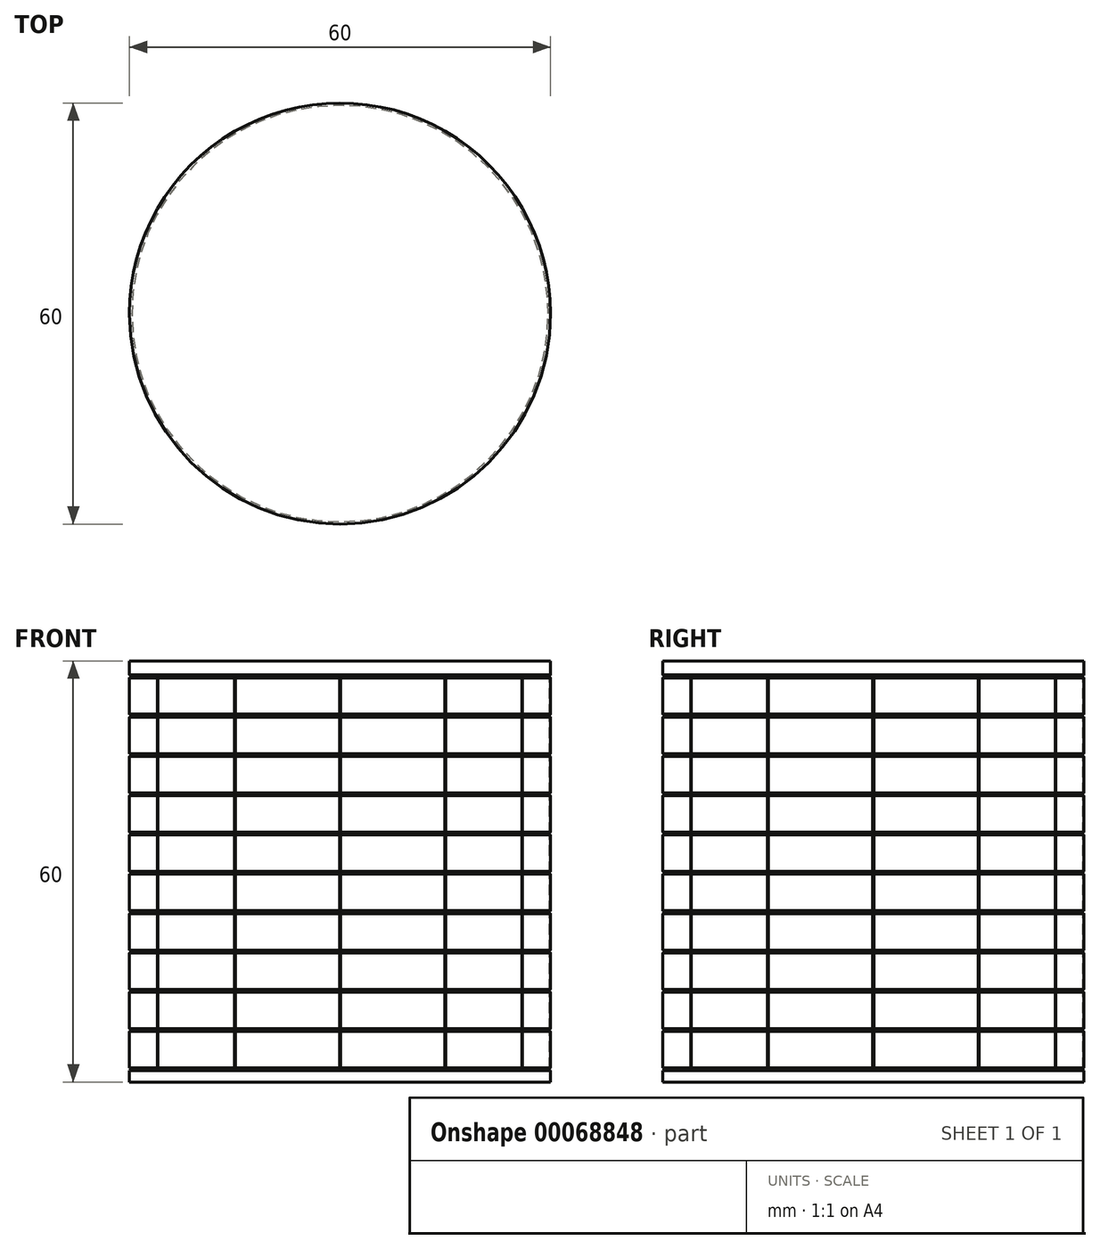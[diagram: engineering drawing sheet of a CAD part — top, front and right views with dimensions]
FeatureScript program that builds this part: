
annotation { "Feature Type Name" : "Feature", "Feature Type Description" : "" }
export const myFeature = defineFeature(function(context is Context, id is Id, definition is map)
    precondition{}
    {
        {
            var Q0;
            Q0=qCreatedBy(makeId("Top.planeOp"),FACE);
            var sketch = newSketch(context, id + "F0", { "sketchPlane" : qUnion([Q0])});
            skCircle(sketch, "E0", {"center": v(0, 0) * mm, "radius": 30 * mm});
            skPoint(sketch, "E1", {"position": v(0, -30) * mm});
            skSolve(sketch);
        }
        {
            var Q0;
            Q0=makeQuery(id+"F0.imprint","IMPRINT",FACE,{"disambiguationData":[TD([[makeQuery(id+"F0.imprint","IMPRINT",EDGE,{"derivedFrom":sQuery(id+"F0.wireOp",EDGE,"E0")}),1.0]])]});
            extrude(context, id + "F1", {"entities" : qUnion([Q0]), "depth" : 60 * mm});
        }
        {
            var Q0;
            Q0=makeQuery(id+"F1.opExtrude","CAP_FACE",FACE,{"disambiguationData":[OSD([sQuery(id+"F0.wireOp",EDGE,"E0")])],"isStart":false});
            var sketch = newSketch(context, id + "F2", { "sketchPlane" : qUnion([Q0])});
            skLineSegment(sketch, "E2", {"start": v(0, -29.87) * mm, "end": v(-0.08, -30) * mm});
            skLineSegment(sketch, "E3", {"start": v(-0.08, -30) * mm, "end": v(0.07, -30) * mm});
            skLineSegment(sketch, "E4", {"start": v(0.07, -30) * mm, "end": v(0, -29.87) * mm});
            skPoint(sketch, "E5", {"position": v(0, -30) * mm});
            skSolve(sketch);
        }
        {
            var Q0;
            Q0 = qSketchRegion(id + "F2", true);
            extrude(context, id + "F3", {"entities" : qUnion([Q0]), "operationType" : NewBodyOperationType.REMOVE, "oppositeDirection" : true, "depth" : 58 * mm, "hasSecondDirection" : true, "secondDirectionOppositeDirection" : true, "secondDirectionDepth" : 2 * mm});
        }
        {
            var Q0;
            Q0=makeQuery(id+"F3.boolean.opBoolean","COPY",FACE,{"derivedFrom":makeQuery(id+"F3.opExtrude","SWEPT_FACE",FACE,{"disambiguationData":[OSD([sQuery(id+"F2.wireOp",EDGE,"E2")])]})});
            var Q1;
            Q1=makeQuery(id+"F3.boolean.opBoolean","COPY",FACE,{"derivedFrom":makeQuery(id+"F3.opExtrude","CAP_FACE",FACE,{"disambiguationData":[OSD([sQuery(id+"F2.wireOp",EDGE,"E2"),sQuery(id+"F2.wireOp",EDGE,"E3"),sQuery(id+"F2.wireOp",EDGE,"E4")])],"isStart":true})});
            var Q2;
            Q2=makeQuery(id+"F3.boolean.opBoolean","COPY",FACE,{"derivedFrom":makeQuery(id+"F3.opExtrude","CAP_FACE",FACE,{"disambiguationData":[OSD([sQuery(id+"F2.wireOp",EDGE,"E2"),sQuery(id+"F2.wireOp",EDGE,"E3"),sQuery(id+"F2.wireOp",EDGE,"E4")])],"isStart":false})});
            var Q3;
            Q3=makeQuery(id+"F3.boolean.opBoolean","COPY",FACE,{"derivedFrom":makeQuery(id+"F3.opExtrude","SWEPT_FACE",FACE,{"disambiguationData":[OSD([sQuery(id+"F2.wireOp",EDGE,"E4")])]})});
            var Q4;
            Q4=makeQuery(id+"F1.opExtrude","CAP_EDGE",EDGE,{"disambiguationData":[OSD([sQuery(id+"F0.wireOp",EDGE,"E0")])],"isStart":true});
            circularPattern(context, id + "F4", {"faces" : qUnion([Q0, Q1, Q2, Q3]), "axis" : qUnion([Q4]), "angle" : 360 * degree, "instanceCount" : 12, "equalSpace" : true, "patternType" : PatternType.FACE});
        }
        {
            var Q0;
            Q0=qCreatedBy(makeId("Right.planeOp"),FACE);
            var sketch = newSketch(context, id + "F5", { "sketchPlane" : qUnion([Q0])});
            skLineSegment(sketch, "E6", {"start": v(-30, 58) * mm, "end": v(-30, 57.6) * mm});
            skLineSegment(sketch, "E7", {"start": v(-30, 57.6) * mm, "end": v(-29.65, 57.8) * mm});
            skLineSegment(sketch, "E8", {"start": v(-29.65, 57.8) * mm, "end": v(-30, 58) * mm});
            skLineSegment(sketch, "E9", {"start": v(-30, 58) * mm, "end": v(-30.1, 58) * mm});
            skLineSegment(sketch, "E10", {"start": v(-30.1, 58) * mm, "end": v(-30.1, 57.6) * mm});
            skLineSegment(sketch, "E11", {"start": v(-30.1, 57.6) * mm, "end": v(-30, 57.6) * mm});
            skLineSegment(sketch, "E12.0.1.0", {"start": v(-30.1, 52.4) * mm, "end": v(-30.1, 52) * mm});
            skLineSegment(sketch, "E12.0.1.1", {"start": v(-30, 52.4) * mm, "end": v(-30, 52) * mm});
            skLineSegment(sketch, "E12.0.1.2", {"start": v(-29.65, 52.2) * mm, "end": v(-30, 52.4) * mm});
            skLineSegment(sketch, "E12.0.1.3", {"start": v(-30, 52.4) * mm, "end": v(-30.1, 52.4) * mm});
            skLineSegment(sketch, "E12.0.1.4", {"start": v(-30, 52) * mm, "end": v(-29.65, 52.2) * mm});
            skLineSegment(sketch, "E12.0.1.5", {"start": v(-30.1, 52) * mm, "end": v(-30, 52) * mm});
            skLineSegment(sketch, "E12.0.2.0", {"start": v(-30.1, 46.8) * mm, "end": v(-30.1, 46.4) * mm});
            skLineSegment(sketch, "E12.0.2.1", {"start": v(-30, 46.8) * mm, "end": v(-30, 46.4) * mm});
            skLineSegment(sketch, "E12.0.2.2", {"start": v(-29.65, 46.6) * mm, "end": v(-30, 46.8) * mm});
            skLineSegment(sketch, "E12.0.2.3", {"start": v(-30, 46.8) * mm, "end": v(-30.1, 46.8) * mm});
            skLineSegment(sketch, "E12.0.2.4", {"start": v(-30, 46.4) * mm, "end": v(-29.65, 46.6) * mm});
            skLineSegment(sketch, "E12.0.2.5", {"start": v(-30.1, 46.4) * mm, "end": v(-30, 46.4) * mm});
            skLineSegment(sketch, "E12.0.3.0", {"start": v(-30.1, 41.2) * mm, "end": v(-30.1, 40.8) * mm});
            skLineSegment(sketch, "E12.0.3.1", {"start": v(-30, 41.2) * mm, "end": v(-30, 40.8) * mm});
            skLineSegment(sketch, "E12.0.3.2", {"start": v(-29.65, 41) * mm, "end": v(-30, 41.2) * mm});
            skLineSegment(sketch, "E12.0.3.3", {"start": v(-30, 41.2) * mm, "end": v(-30.1, 41.2) * mm});
            skLineSegment(sketch, "E12.0.3.4", {"start": v(-30, 40.8) * mm, "end": v(-29.65, 41) * mm});
            skLineSegment(sketch, "E12.0.3.5", {"start": v(-30.1, 40.8) * mm, "end": v(-30, 40.8) * mm});
            skLineSegment(sketch, "E12.0.4.0", {"start": v(-30.1, 35.6) * mm, "end": v(-30.1, 35.2) * mm});
            skLineSegment(sketch, "E12.0.4.1", {"start": v(-30, 35.6) * mm, "end": v(-30, 35.2) * mm});
            skLineSegment(sketch, "E12.0.4.2", {"start": v(-29.65, 35.4) * mm, "end": v(-30, 35.6) * mm});
            skLineSegment(sketch, "E12.0.4.3", {"start": v(-30, 35.6) * mm, "end": v(-30.1, 35.6) * mm});
            skLineSegment(sketch, "E12.0.4.4", {"start": v(-30, 35.2) * mm, "end": v(-29.65, 35.4) * mm});
            skLineSegment(sketch, "E12.0.4.5", {"start": v(-30.1, 35.2) * mm, "end": v(-30, 35.2) * mm});
            skLineSegment(sketch, "E12.0.5.0", {"start": v(-30.1, 30) * mm, "end": v(-30.1, 29.6) * mm});
            skLineSegment(sketch, "E12.0.5.1", {"start": v(-30, 30) * mm, "end": v(-30, 29.6) * mm});
            skLineSegment(sketch, "E12.0.5.2", {"start": v(-29.65, 29.8) * mm, "end": v(-30, 30) * mm});
            skLineSegment(sketch, "E12.0.5.3", {"start": v(-30, 30) * mm, "end": v(-30.1, 30) * mm});
            skLineSegment(sketch, "E12.0.5.4", {"start": v(-30, 29.6) * mm, "end": v(-29.65, 29.8) * mm});
            skLineSegment(sketch, "E12.0.5.5", {"start": v(-30.1, 29.6) * mm, "end": v(-30, 29.6) * mm});
            skLineSegment(sketch, "E12.0.6.0", {"start": v(-30.1, 24.4) * mm, "end": v(-30.1, 24) * mm});
            skLineSegment(sketch, "E12.0.6.1", {"start": v(-30, 24.4) * mm, "end": v(-30, 24) * mm});
            skLineSegment(sketch, "E12.0.6.2", {"start": v(-29.65, 24.2) * mm, "end": v(-30, 24.4) * mm});
            skLineSegment(sketch, "E12.0.6.3", {"start": v(-30, 24.4) * mm, "end": v(-30.1, 24.4) * mm});
            skLineSegment(sketch, "E12.0.6.4", {"start": v(-30, 24) * mm, "end": v(-29.65, 24.2) * mm});
            skLineSegment(sketch, "E12.0.6.5", {"start": v(-30.1, 24) * mm, "end": v(-30, 24) * mm});
            skLineSegment(sketch, "E12.0.7.0", {"start": v(-30.1, 18.8) * mm, "end": v(-30.1, 18.4) * mm});
            skLineSegment(sketch, "E12.0.7.1", {"start": v(-30, 18.8) * mm, "end": v(-30, 18.4) * mm});
            skLineSegment(sketch, "E12.0.7.2", {"start": v(-29.65, 18.6) * mm, "end": v(-30, 18.8) * mm});
            skLineSegment(sketch, "E12.0.7.3", {"start": v(-30, 18.8) * mm, "end": v(-30.1, 18.8) * mm});
            skLineSegment(sketch, "E12.0.7.4", {"start": v(-30, 18.4) * mm, "end": v(-29.65, 18.6) * mm});
            skLineSegment(sketch, "E12.0.7.5", {"start": v(-30.1, 18.4) * mm, "end": v(-30, 18.4) * mm});
            skLineSegment(sketch, "E12.0.8.0", {"start": v(-30.1, 13.2) * mm, "end": v(-30.1, 12.8) * mm});
            skLineSegment(sketch, "E12.0.8.1", {"start": v(-30, 13.2) * mm, "end": v(-30, 12.8) * mm});
            skLineSegment(sketch, "E12.0.8.2", {"start": v(-29.65, 13) * mm, "end": v(-30, 13.2) * mm});
            skLineSegment(sketch, "E12.0.8.3", {"start": v(-30, 13.2) * mm, "end": v(-30.1, 13.2) * mm});
            skLineSegment(sketch, "E12.0.8.4", {"start": v(-30, 12.8) * mm, "end": v(-29.65, 13) * mm});
            skLineSegment(sketch, "E12.0.8.5", {"start": v(-30.1, 12.8) * mm, "end": v(-30, 12.8) * mm});
            skLineSegment(sketch, "E12.0.9.0", {"start": v(-30.1, 7.6) * mm, "end": v(-30.1, 7.2) * mm});
            skLineSegment(sketch, "E12.0.9.1", {"start": v(-30, 7.6) * mm, "end": v(-30, 7.2) * mm});
            skLineSegment(sketch, "E12.0.9.2", {"start": v(-29.65, 7.4) * mm, "end": v(-30, 7.6) * mm});
            skLineSegment(sketch, "E12.0.9.3", {"start": v(-30, 7.6) * mm, "end": v(-30.1, 7.6) * mm});
            skLineSegment(sketch, "E12.0.9.4", {"start": v(-30, 7.2) * mm, "end": v(-29.65, 7.4) * mm});
            skLineSegment(sketch, "E12.0.9.5", {"start": v(-30.1, 7.2) * mm, "end": v(-30, 7.2) * mm});
            skLineSegment(sketch, "E12.direction1", {"start": v(-30.1, 57.6) * mm, "end": v(-5.05, 57.6) * mm, "construction": true});
            skLineSegment(sketch, "E12.direction2", {"start": v(-30.1, 57.6) * mm, "end": v(-30.1, 52) * mm, "construction": true});
            skLineSegment(sketch, "E13.0.0.10", {"start": v(-30.1, 2) * mm, "end": v(-30.1, 1.6) * mm});
            skLineSegment(sketch, "E13.3.0.10", {"start": v(-30, 2) * mm, "end": v(-30, 1.6) * mm});
            skLineSegment(sketch, "E13.6.0.10", {"start": v(-29.65, 1.8) * mm, "end": v(-30, 2) * mm});
            skLineSegment(sketch, "E13.9.0.10", {"start": v(-30, 2) * mm, "end": v(-30.1, 2) * mm});
            skLineSegment(sketch, "E13.12.0.10", {"start": v(-30, 1.6) * mm, "end": v(-29.65, 1.8) * mm});
            skLineSegment(sketch, "E13.15.0.10", {"start": v(-30.1, 1.6) * mm, "end": v(-30, 1.6) * mm});
            skSolve(sketch);
        }
        {
            var Q0;
            Q0 = qSketchRegion(id + "F5", true);
            var Q1;
            Q1=makeQuery(id+"F1.opExtrude","CAP_EDGE",EDGE,{"disambiguationData":[OSD([sQuery(id+"F0.wireOp",EDGE,"E0")])],"isStart":false});
            revolve(context, id + "F6", {"operationType" : NewBodyOperationType.REMOVE, "entities" : qUnion([Q0]), "axis" : qUnion([Q1]), "revolveType" : RevolveType.FULL, "oppositeDirection" : true});
        }
    });
